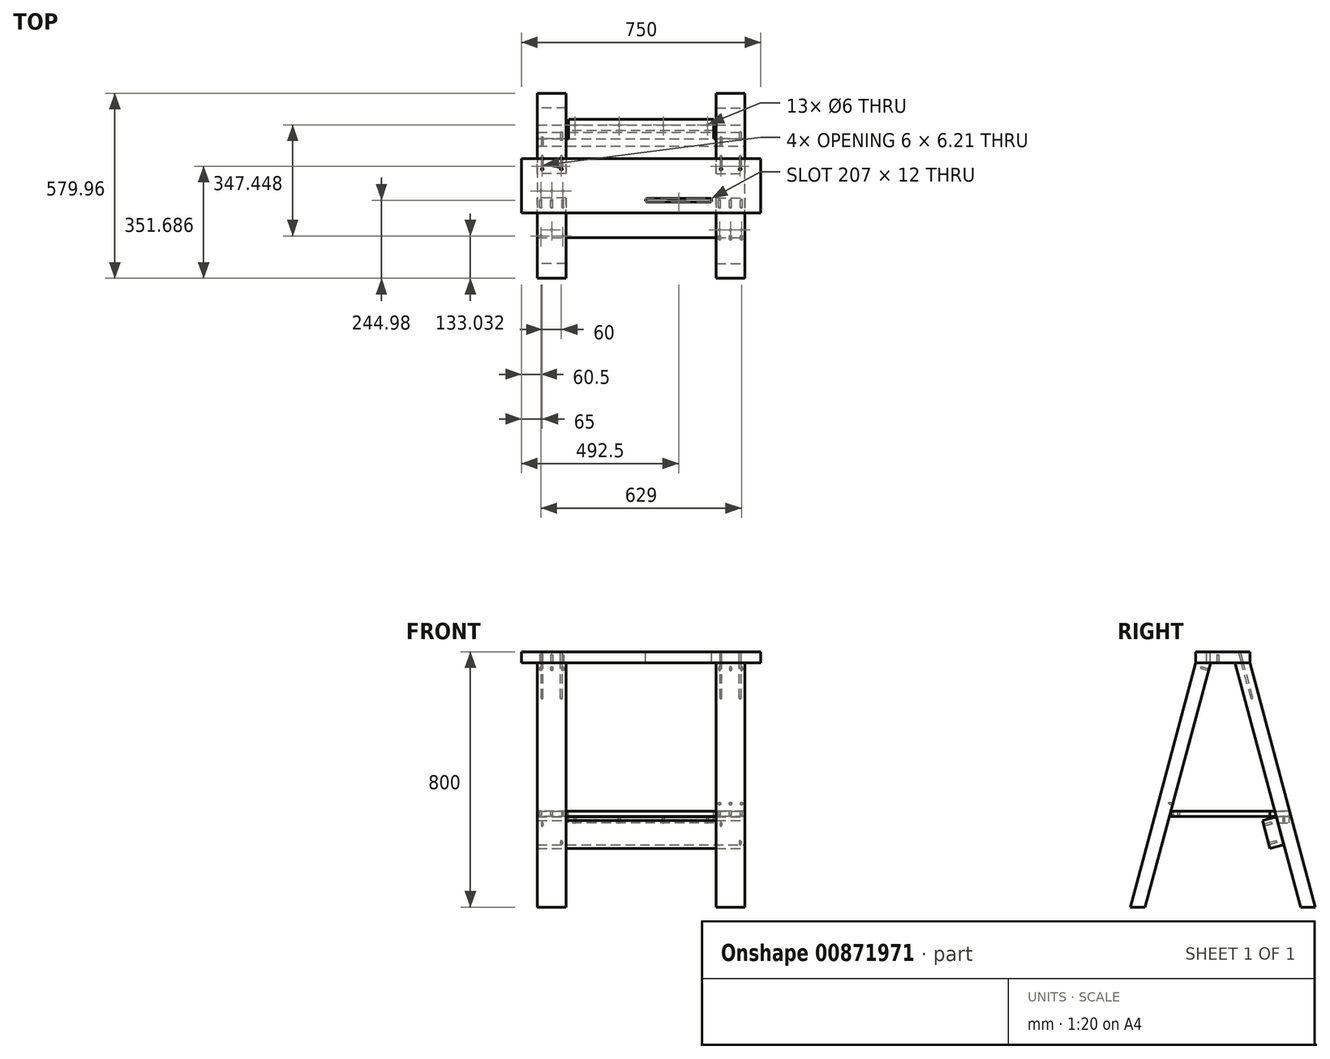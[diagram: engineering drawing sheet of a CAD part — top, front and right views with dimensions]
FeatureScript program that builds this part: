
annotation { "Feature Type Name" : "Feature", "Feature Type Description" : "" }
export const myFeature = defineFeature(function(context is Context, id is Id, definition is map)
    precondition{}
    {
        {
            var Q0;
            Q0=qCreatedBy(makeId("Right.planeOp"),FACE);
            var sketch = newSketch(context, id + "F0", { "sketchPlane" : qUnion([Q0])});
            skLineSegment(sketch, "E0.bottom", {"start": v(-85, -17.5) * mm, "end": v(85, -17.5) * mm});
            skLineSegment(sketch, "E0.top", {"start": v(-85, 17.5) * mm, "end": v(85, 17.5) * mm});
            skLineSegment(sketch, "E0.left", {"start": v(-85, -17.5) * mm, "end": v(-85, 17.5) * mm});
            skLineSegment(sketch, "E0.right", {"start": v(85, -17.5) * mm, "end": v(85, 17.5) * mm});
            skPoint(sketch, "E0.middle", {"position": v(0, 0) * mm});
            skSolve(sketch);
        }
        {
            var Q0;
            Q0=makeQuery(id+"F0.imprint","IMPRINT",FACE,{"disambiguationData":[TD([[makeQuery(id+"F0.imprint","IMPRINT",EDGE,{"derivedFrom":sQuery(id+"F0.wireOp",EDGE,"E0.bottom")}),1.0]])]});
            extrude(context, id + "F1", {"entities" : qUnion([Q0]), "endBound" : BoundingType.SYMMETRIC, "depth" : 750 * mm, "offsetDistance" : 25 * mm});
        }
        {
            var Q0;
            Q0=qCreatedBy(makeId("Front.planeOp"),FACE);
            var sketch = newSketch(context, id + "F2", { "sketchPlane" : qUnion([Q0])});
            skLineSegment(sketch, "E1", {"start": v(-325, -212.53) * mm, "end": v(-325, -17.5) * mm});
            skLineSegment(sketch, "E2", {"start": v(-325, -17.5) * mm, "end": v(-325, -257.51) * mm, "construction": true});
            skSolve(sketch);
        }
        {
            var Q0;
            Q0=qCreatedBy(makeId("Right.planeOp"),FACE);
            var Q1;
            Q1=sQuery(id+"F2.wireOp",EDGE,"E2");
            cPlane(context, id + "F3", {"entities" : qUnion([Q0, Q1]), "cplaneType" : CPlaneType.LINE_ANGLE, "offset" : 25 * mm, "angle" : 0 * degree, "width" : 150 * mm, "height" : 150 * mm});
        }
        {
            var Q0;
            Q0=qCreatedBy(id+"F3.planeOp",FACE);
            var sketch = newSketch(context, id + "F4", { "sketchPlane" : qUnion([Q0])});
            skLineSegment(sketch, "E3", {"start": v(-85, -17.5) * mm, "end": v(-289.98, -782.5) * mm});
            skLineSegment(sketch, "E4", {"start": v(-289.98, -782.5) * mm, "end": v(-243.4, -782.5) * mm});
            skLineSegment(sketch, "E5", {"start": v(-243.4, -782.5) * mm, "end": v(-38.41, -17.5) * mm});
            skLineSegment(sketch, "E6", {"start": v(-38.41, -17.5) * mm, "end": v(-85, -17.5) * mm});
            skLineSegment(sketch, "E7", {"start": v(0, 0) * mm, "end": v(0, -726.6) * mm, "construction": true});
            skSolve(sketch);
        }
        {
            var Q0;
            Q0 = qSketchRegion(id + "F4", true);
            extrude(context, id + "F5", {"entities" : qUnion([Q0]), "oppositeDirection" : true, "depth" : 90 * mm, "offsetDistance" : 25 * mm});
        }
        {
            var Q0;
            Q0=makeQuery(id+"F5.opExtrude","SWEPT_BODY",BODY,{"disambiguationData":[OSD([sQuery(id+"F4.wireOp",EDGE,"E3"),sQuery(id+"F4.wireOp",EDGE,"E4"),sQuery(id+"F4.wireOp",EDGE,"E5"),sQuery(id+"F4.wireOp",EDGE,"E6")])]});
            var Q1;
            Q1=qCreatedBy(makeId("Front.planeOp"),FACE);
            mirror(context, id + "F6", {"entities" : qUnion([Q0]), "mirrorPlane" : qUnion([Q1])});
        }
        {
            var Q0;
            Q0=makeQuery(id+"F6.opPattern","COPY",FACE,{"derivedFrom":makeQuery(id+"F5.opExtrude","SWEPT_FACE",FACE,{"disambiguationData":[OSD([sQuery(id+"F4.wireOp",EDGE,"E5")])]}),"instanceName":"1"});
            var sketch = newSketch(context, id + "F7", { "sketchPlane" : qUnion([Q0])});
            skPoint(sketch, "E8", {"position": v(245.5, -48.65) * mm});
            skPoint(sketch, "E9", {"position": v(280, -48.65) * mm});
            skPoint(sketch, "E10", {"position": v(314.5, -48.65) * mm});
            skLineSegment(sketch, "E11", {"start": v(280, -48.65) * mm, "end": v(245.5, -48.65) * mm, "construction": true});
            skLineSegment(sketch, "E12", {"start": v(280, -48.65) * mm, "end": v(314.5, -48.65) * mm, "construction": true});
            skLineSegment(sketch, "E13", {"start": v(280, -48.65) * mm, "end": v(280, -26.85) * mm, "construction": true});
            skSolve(sketch);
        }
        {
            var Q0;
            Q0=sQuery(id+"F7.wireOp",VERTEX,"E8");
            var Q1;
            Q1=sQuery(id+"F7.wireOp",VERTEX,"E9");
            var Q2;
            Q2=sQuery(id+"F7.wireOp",VERTEX,"E10");
            var Q3;
            Q3=makeQuery(id+"F6.opPattern","COPY",BODY,{"derivedFrom":makeQuery(id+"F5.opExtrude","SWEPT_BODY",BODY,{"disambiguationData":[OSD([sQuery(id+"F4.wireOp",EDGE,"E3"),sQuery(id+"F4.wireOp",EDGE,"E4"),sQuery(id+"F4.wireOp",EDGE,"E5"),sQuery(id+"F4.wireOp",EDGE,"E6")])]}),"instanceName":"1"});
            hole(context, id + "F8", {"style" : HoleStyle.SIMPLE, "endStyle" : HoleEndStyle.BLIND, "holeDiameter" : 6 * mm, "majorDiameter" : 5 * mm, "holeDepth" : 25 * mm, "isTappedThrough" : true, "tappedDepth" : 12 * mm, "tapClearance" : 3, "locations" : qUnion([Q0, Q1, Q2]), "scope" : qUnion([Q3])});
        }
        {
            var Q0;
            Q0=makeQuery(id+"F6.opPattern","COPY",BODY,{"derivedFrom":makeQuery(id+"F5.opExtrude","SWEPT_BODY",BODY,{"disambiguationData":[OSD([sQuery(id+"F4.wireOp",EDGE,"E3"),sQuery(id+"F4.wireOp",EDGE,"E4"),sQuery(id+"F4.wireOp",EDGE,"E5"),sQuery(id+"F4.wireOp",EDGE,"E6")])]}),"instanceName":"1"});
            var Q1;
            Q1=makeQuery(id+"F5.opExtrude","SWEPT_BODY",BODY,{"disambiguationData":[OSD([sQuery(id+"F4.wireOp",EDGE,"E3"),sQuery(id+"F4.wireOp",EDGE,"E4"),sQuery(id+"F4.wireOp",EDGE,"E5"),sQuery(id+"F4.wireOp",EDGE,"E6")])]});
            var Q2;
            Q2=qCreatedBy(makeId("Right.planeOp"),FACE);
            mirror(context, id + "F9", {"entities" : qUnion([Q0, Q1]), "mirrorPlane" : qUnion([Q2])});
        }
        {
            var Q0;
            Q0=makeQuery(id+"F1.opExtrude","SWEPT_FACE",FACE,{"disambiguationData":[OSD([sQuery(id+"F0.wireOp",EDGE,"E0.bottom")])]});
            var sketch = newSketch(context, id + "F10", { "sketchPlane" : qUnion([Q0])});
            skPoint(sketch, "E14", {"position": v(-245.5, 16) * mm});
            skPoint(sketch, "E15", {"position": v(-280, 16) * mm});
            skPoint(sketch, "E16", {"position": v(-314.5, 16) * mm});
            skLineSegment(sketch, "E17", {"start": v(-314.5, 16) * mm, "end": v(-314.5, 44.05) * mm, "construction": true});
            skLineSegment(sketch, "E18", {"start": v(-245.5, 44.05) * mm, "end": v(-245.5, 16) * mm, "construction": true});
            skLineSegment(sketch, "E19", {"start": v(-280, 16) * mm, "end": v(-280, 44.05) * mm, "construction": true});
            skLineSegment(sketch, "E20", {"start": v(-375, 0) * mm, "end": v(-119.6, 0) * mm, "construction": true});
            skSolve(sketch);
        }
        {
            var Q0;
            Q0=sQuery(id+"F10.wireOp",VERTEX,"E16");
            var Q1;
            Q1=sQuery(id+"F10.wireOp",VERTEX,"E15");
            var Q2;
            Q2=sQuery(id+"F10.wireOp",VERTEX,"E14");
            var Q3;
            Q3=makeQuery(id+"F1.opExtrude","SWEPT_BODY",BODY,{"disambiguationData":[OSD([sQuery(id+"F0.wireOp",EDGE,"E0.bottom"),sQuery(id+"F0.wireOp",EDGE,"E0.top"),sQuery(id+"F0.wireOp",EDGE,"E0.left"),sQuery(id+"F0.wireOp",EDGE,"E0.right")])]});
            hole(context, id + "F11", {"style" : HoleStyle.SIMPLE, "endStyle" : HoleEndStyle.BLIND, "holeDiameter" : 6 * mm, "majorDiameter" : 5 * mm, "holeDepth" : 25 * mm, "isTappedThrough" : true, "tappedDepth" : 12 * mm, "tapClearance" : 3, "locations" : qUnion([Q0, Q1, Q2]), "scope" : qUnion([Q3])});
        }
        {
            var Q0;
            Q0=qCreatedBy(makeId("Right.planeOp"),FACE);
            var sketch = newSketch(context, id + "F12", { "sketchPlane" : qUnion([Q0])});
            skLineSegment(sketch, "E21", {"start": v(-274.26, -482.5) * mm, "end": v(250.79, -482.5) * mm});
            skSolve(sketch);
        }
        {
            var Q0;
            Q0=sQuery(id+"F12.wireOp",EDGE,"E21");
            var Q1;
            Q1=qCreatedBy(makeId("Top.planeOp"),FACE);
            cPlane(context, id + "F13", {"entities" : qUnion([Q0, Q1]), "cplaneType" : CPlaneType.LINE_ANGLE, "offset" : 25 * mm, "angle" : 0 * degree, "width" : 150 * mm, "height" : 150 * mm});
        }
        {
            var Q0;
            Q0=qCreatedBy(id+"F13.planeOp",FACE);
            var sketch = newSketch(context, id + "F14", { "sketchPlane" : qUnion([Q0])});
            skLineSegment(sketch, "E22", {"start": v(-325, 162) * mm, "end": v(325, 162) * mm});
            skLineSegment(sketch, "E23", {"start": v(325, 162) * mm, "end": v(325, -148) * mm});
            skLineSegment(sketch, "E24", {"start": v(325, -148) * mm, "end": v(227.5, -148) * mm});
            skLineSegment(sketch, "E25", {"start": v(227.5, -148) * mm, "end": v(227.5, -208) * mm});
            skLineSegment(sketch, "E26", {"start": v(227.5, -208) * mm, "end": v(-227.5, -208) * mm});
            skLineSegment(sketch, "E27", {"start": v(-227.5, -208) * mm, "end": v(-227.5, -148) * mm});
            skLineSegment(sketch, "E28", {"start": v(-227.5, -148) * mm, "end": v(-325, -148) * mm});
            skLineSegment(sketch, "E29", {"start": v(-325, -148) * mm, "end": v(-325, 162) * mm});
            skLineSegment(sketch, "E30", {"start": v(0, 0) * mm, "end": v(0, 162) * mm, "construction": true});
            skSolve(sketch);
        }
        {
            var Q0;
            Q0 = qSketchRegion(id + "F14", true);
            extrude(context, id + "F15", {"entities" : qUnion([Q0]), "depth" : 16 * mm, "offsetDistance" : 25 * mm});
        }
        {
            var Q0;
            Q0=makeQuery(id+"F9.opPattern","COPY",FACE,{"derivedFrom":makeQuery(id+"F6.opPattern","COPY",FACE,{"derivedFrom":makeQuery(id+"F5.opExtrude","SWEPT_FACE",FACE,{"disambiguationData":[OSD([sQuery(id+"F4.wireOp",EDGE,"E5")])]}),"instanceName":"1"}),"instanceName":"1"});
            var sketch = newSketch(context, id + "F16", { "sketchPlane" : qUnion([Q0])});
            skLineSegment(sketch, "E31", {"start": v(-314.5, -484.83) * mm, "end": v(-280, -484.83) * mm, "construction": true});
            skLineSegment(sketch, "E32", {"start": v(-280, -484.83) * mm, "end": v(-245.5, -484.83) * mm, "construction": true});
            skLineSegment(sketch, "E33", {"start": v(-245.5, -484.83) * mm, "end": v(-245.5, -21.04) * mm, "construction": true});
            skLineSegment(sketch, "E34", {"start": v(-314.5, -21.04) * mm, "end": v(-314.5, -484.83) * mm, "construction": true});
            skSolve(sketch);
        }
        {
            var Q0;
            Q0=sQuery(id+"F16.wireOp",VERTEX,"E31.start");
            var Q1;
            Q1=sQuery(id+"F16.wireOp",VERTEX,"E31.end");
            var Q2;
            Q2=sQuery(id+"F16.wireOp",VERTEX,"E32.end");
            var Q3;
            Q3=makeQuery(id+"F9.opPattern","COPY",BODY,{"derivedFrom":makeQuery(id+"F6.opPattern","COPY",BODY,{"derivedFrom":makeQuery(id+"F5.opExtrude","SWEPT_BODY",BODY,{"disambiguationData":[OSD([sQuery(id+"F4.wireOp",EDGE,"E3"),sQuery(id+"F4.wireOp",EDGE,"E4"),sQuery(id+"F4.wireOp",EDGE,"E5"),sQuery(id+"F4.wireOp",EDGE,"E6")])]}),"instanceName":"1"}),"instanceName":"1"});
            var Q4;
            Q4=makeQuery(id+"F6.opPattern","COPY",BODY,{"derivedFrom":makeQuery(id+"F5.opExtrude","SWEPT_BODY",BODY,{"disambiguationData":[OSD([sQuery(id+"F4.wireOp",EDGE,"E3"),sQuery(id+"F4.wireOp",EDGE,"E4"),sQuery(id+"F4.wireOp",EDGE,"E5"),sQuery(id+"F4.wireOp",EDGE,"E6")])]}),"instanceName":"1"});
            hole(context, id + "F17", {"style" : HoleStyle.SIMPLE, "endStyle" : HoleEndStyle.BLIND, "holeDiameter" : 6 * mm, "majorDiameter" : 5 * mm, "holeDepth" : 12 * mm, "isTappedThrough" : true, "tappedDepth" : 12 * mm, "tapClearance" : 3, "locations" : qUnion([Q0, Q1, Q2]), "scope" : qUnion([Q3, Q4])});
        }
        {
            var Q0;
            Q0=makeQuery(id+"F15.opExtrude","CAP_FACE",FACE,{"disambiguationData":[OSD([sQuery(id+"F14.wireOp",EDGE,"E22"),sQuery(id+"F14.wireOp",EDGE,"E23"),sQuery(id+"F14.wireOp",EDGE,"E24"),sQuery(id+"F14.wireOp",EDGE,"E25"),sQuery(id+"F14.wireOp",EDGE,"E26"),sQuery(id+"F14.wireOp",EDGE,"E27"),sQuery(id+"F14.wireOp",EDGE,"E28"),sQuery(id+"F14.wireOp",EDGE,"E29")])],"isStart":true});
            var sketch = newSketch(context, id + "F18", { "sketchPlane" : qUnion([Q0])});
            skLineSegment(sketch, "E35", {"start": v(314.5, -138) * mm, "end": v(280, -138) * mm});
            skLineSegment(sketch, "E36", {"start": v(280, -138) * mm, "end": v(245.5, -138) * mm});
            skLineSegment(sketch, "E37", {"start": v(245.5, -138) * mm, "end": v(-245.5, -138) * mm});
            skLineSegment(sketch, "E38", {"start": v(-245.5, -138) * mm, "end": v(-280, -138) * mm});
            skLineSegment(sketch, "E39", {"start": v(-280, -138) * mm, "end": v(-314.5, -138) * mm});
            skLineSegment(sketch, "E40", {"start": v(314.5, -156.95) * mm, "end": v(314.5, -138) * mm});
            skLineSegment(sketch, "E41", {"start": v(245.5, -156.95) * mm, "end": v(245.5, -138) * mm});
            skLineSegment(sketch, "E42", {"start": v(-245.5, -156.95) * mm, "end": v(-245.5, -138) * mm});
            skLineSegment(sketch, "E43", {"start": v(-314.5, -156.95) * mm, "end": v(-314.5, -138) * mm});
            skSolve(sketch);
        }
        {
            var Q0;
            Q0=sQuery(id+"F18.wireOp",VERTEX,"E43.start");
            var Q1;
            Q1=sQuery(id+"F18.wireOp",VERTEX,"E38.end");
            var Q2;
            Q2=sQuery(id+"F18.wireOp",VERTEX,"E42.start");
            var Q3;
            Q3=sQuery(id+"F18.wireOp",VERTEX,"E37.start");
            var Q4;
            Q4=sQuery(id+"F18.wireOp",VERTEX,"E36.start");
            var Q5;
            Q5=sQuery(id+"F18.wireOp",VERTEX,"E35.start");
            var Q6;
            Q6=makeQuery(id+"F15.opExtrude","SWEPT_BODY",BODY,{"disambiguationData":[OSD([sQuery(id+"F14.wireOp",EDGE,"E22"),sQuery(id+"F14.wireOp",EDGE,"E23"),sQuery(id+"F14.wireOp",EDGE,"E24"),sQuery(id+"F14.wireOp",EDGE,"E25"),sQuery(id+"F14.wireOp",EDGE,"E26"),sQuery(id+"F14.wireOp",EDGE,"E27"),sQuery(id+"F14.wireOp",EDGE,"E28"),sQuery(id+"F14.wireOp",EDGE,"E29")])]});
            hole(context, id + "F19", {"style" : HoleStyle.SIMPLE, "endStyle" : HoleEndStyle.BLIND, "holeDiameter" : 6 * mm, "majorDiameter" : 5 * mm, "holeDepth" : 12 * mm, "isTappedThrough" : true, "tappedDepth" : 12 * mm, "tapClearance" : 3, "locations" : qUnion([Q0, Q1, Q2, Q3, Q4, Q5]), "scope" : qUnion([Q6])});
        }
        {
            var Q0;
            Q0=makeQuery(id+"F5.opExtrude","SWEPT_FACE",FACE,{"disambiguationData":[OSD([sQuery(id+"F4.wireOp",EDGE,"E5")])]});
            var sketch = newSketch(context, id + "F20", { "sketchPlane" : qUnion([Q0])});
            skLineSegment(sketch, "E44.bottom", {"start": v(-325, -526.33) * mm, "end": v(325, -526.33) * mm});
            skLineSegment(sketch, "E44.top", {"start": v(-325, -616.33) * mm, "end": v(325, -616.33) * mm});
            skLineSegment(sketch, "E44.left", {"start": v(-325, -526.33) * mm, "end": v(-325, -616.33) * mm});
            skLineSegment(sketch, "E44.right", {"start": v(325, -526.33) * mm, "end": v(325, -616.33) * mm});
            skSolve(sketch);
        }
        {
            var Q0;
            {var subQ0=sQuery(id+"F20.wireOp",EDGE,"E44.right");Q0=makeQuery(id+"F20.imprint","IMPRINT",FACE,{"disambiguationData":[TD([[makeQuery(id+"F20.imprint","IMPRINT",EDGE,{"derivedFrom":subQ0}),-1.0]])]});}
            var Q1;
            {var subQ0=sQuery(id+"F20.wireOp",EDGE,"E44.left");Q1=makeQuery(id+"F20.imprint","IMPRINT",FACE,{"disambiguationData":[TD([[makeQuery(id+"F20.imprint","IMPRINT",EDGE,{"derivedFrom":subQ0}),-1.0]])]});}
            extrude(context, id + "F21", {"entities" : qUnion([Q0, Q1]), "depth" : 45 * mm, "offsetDistance" : 25 * mm});
        }
        {
            var Q0;
            Q0=makeQuery(id+"F15.opExtrude","CAP_FACE",FACE,{"disambiguationData":[OSD([sQuery(id+"F14.wireOp",EDGE,"E22"),sQuery(id+"F14.wireOp",EDGE,"E23"),sQuery(id+"F14.wireOp",EDGE,"E24"),sQuery(id+"F14.wireOp",EDGE,"E25"),sQuery(id+"F14.wireOp",EDGE,"E26"),sQuery(id+"F14.wireOp",EDGE,"E27"),sQuery(id+"F14.wireOp",EDGE,"E28"),sQuery(id+"F14.wireOp",EDGE,"E29")])],"isStart":false});
            var sketch = newSketch(context, id + "F22", { "sketchPlane" : qUnion([Q0])});
            skLineSegment(sketch, "E45.bottom", {"start": v(227.5, -208) * mm, "end": v(-227.5, -208) * mm});
            skLineSegment(sketch, "E45.top", {"start": v(227.5, -173) * mm, "end": v(-227.5, -173) * mm});
            skLineSegment(sketch, "E45.left", {"start": v(227.5, -208) * mm, "end": v(227.5, -173) * mm});
            skLineSegment(sketch, "E45.right", {"start": v(-227.5, -208) * mm, "end": v(-227.5, -173) * mm});
            skSolve(sketch);
        }
        {
            var Q0;
            Q0 = qSketchRegion(id + "F22", true);
            extrude(context, id + "F23", {"entities" : qUnion([Q0]), "depth" : 20 * mm, "offsetDistance" : 25 * mm});
        }
        {
            var Q0;
            Q0=makeQuery(id+"F21.opExtrude","CAP_FACE",FACE,{"disambiguationData":[OSD([sQuery(id+"F4.wireOp",EDGE,"E5"),sQuery(id+"F20.wireOp",EDGE,"E44.bottom"),sQuery(id+"F20.wireOp",EDGE,"E44.top"),sQuery(id+"F20.wireOp",EDGE,"E44.right")])],"isStart":false});
            var sketch = newSketch(context, id + "F24", { "sketchPlane" : qUnion([Q0])});
            skLineSegment(sketch, "E46", {"start": v(250, -541.33) * mm, "end": v(310, -601.33) * mm});
            skLineSegment(sketch, "E47", {"start": v(-310, -541.33) * mm, "end": v(-250, -601.33) * mm});
            skSolve(sketch);
        }
        {
            var Q0;
            Q0=sQuery(id+"F24.wireOp",VERTEX,"E46.start");
            var Q1;
            Q1=sQuery(id+"F24.wireOp",VERTEX,"E46.end");
            var Q2;
            Q2=sQuery(id+"F24.wireOp",VERTEX,"E47.start");
            var Q3;
            Q3=sQuery(id+"F24.wireOp",VERTEX,"E47.end");
            var Q4;
            Q4=makeQuery(id+"F21.opExtrude","SWEPT_BODY",BODY,{"disambiguationData":[OSD([sQuery(id+"F4.wireOp",EDGE,"E5"),sQuery(id+"F20.wireOp",EDGE,"E44.bottom"),sQuery(id+"F20.wireOp",EDGE,"E44.top"),sQuery(id+"F20.wireOp",EDGE,"E44.right")])]});
            hole(context, id + "F25", {"style" : HoleStyle.SIMPLE, "endStyle" : HoleEndStyle.BLIND, "holeDiameter" : 6 * mm, "majorDiameter" : 5 * mm, "holeDepth" : 25 * mm, "isTappedThrough" : true, "tappedDepth" : 12 * mm, "tapClearance" : 3, "locations" : qUnion([Q0, Q1, Q2, Q3]), "scope" : qUnion([Q4])});
        }
        {
            var Q0;
            Q0=makeQuery(id+"F23.opExtrude","CAP_FACE",FACE,{"disambiguationData":[OSD([sQuery(id+"F22.wireOp",EDGE,"E45.bottom"),sQuery(id+"F22.wireOp",EDGE,"E45.top"),sQuery(id+"F22.wireOp",EDGE,"E45.left"),sQuery(id+"F22.wireOp",EDGE,"E45.right")])],"isStart":false});
            var sketch = newSketch(context, id + "F26", { "sketchPlane" : qUnion([Q0])});
            skLineSegment(sketch, "E48", {"start": v(207.5, -190.5) * mm, "end": v(69.17, -190.5) * mm});
            skLineSegment(sketch, "E49", {"start": v(69.17, -190.5) * mm, "end": v(-69.17, -190.5) * mm});
            skLineSegment(sketch, "E50", {"start": v(-69.17, -190.5) * mm, "end": v(-207.5, -190.5) * mm});
            skSolve(sketch);
        }
        {
            var Q0;
            Q0=sQuery(id+"F26.wireOp",VERTEX,"E48.start");
            var Q1;
            Q1=sQuery(id+"F26.wireOp",VERTEX,"E48.end");
            var Q2;
            Q2=sQuery(id+"F26.wireOp",VERTEX,"E49.end");
            var Q3;
            Q3=sQuery(id+"F26.wireOp",VERTEX,"E50.end");
            var Q4;
            Q4=makeQuery(id+"F15.opExtrude","SWEPT_BODY",BODY,{"disambiguationData":[OSD([sQuery(id+"F14.wireOp",EDGE,"E22"),sQuery(id+"F14.wireOp",EDGE,"E23"),sQuery(id+"F14.wireOp",EDGE,"E24"),sQuery(id+"F14.wireOp",EDGE,"E25"),sQuery(id+"F14.wireOp",EDGE,"E26"),sQuery(id+"F14.wireOp",EDGE,"E27"),sQuery(id+"F14.wireOp",EDGE,"E28"),sQuery(id+"F14.wireOp",EDGE,"E29")])]});
            var Q5;
            Q5=makeQuery(id+"F23.opExtrude","SWEPT_BODY",BODY,{"disambiguationData":[OSD([sQuery(id+"F22.wireOp",EDGE,"E45.bottom"),sQuery(id+"F22.wireOp",EDGE,"E45.top"),sQuery(id+"F22.wireOp",EDGE,"E45.left"),sQuery(id+"F22.wireOp",EDGE,"E45.right")])]});
            hole(context, id + "F27", {"style" : HoleStyle.SIMPLE, "endStyle" : HoleEndStyle.BLIND, "holeDiameter" : 6 * mm, "majorDiameter" : 5 * mm, "holeDepth" : 20 * mm, "isTappedThrough" : true, "tappedDepth" : 12 * mm, "tapClearance" : 3, "locations" : qUnion([Q0, Q1, Q2, Q3]), "scope" : qUnion([Q4, Q5])});
        }
        {
            var Q0;
            Q0=qCreatedBy(makeId("Right.planeOp"),FACE);
            var sketch = newSketch(context, id + "F28", { "sketchPlane" : qUnion([Q0])});
            skLineSegment(sketch, "E51", {"start": v(29.03, 17.5) * mm, "end": v(72.5, 29.15) * mm, "construction": true});
            skSolve(sketch);
        }
        {
            var Q0;
            Q0=sQuery(id+"F28.wireOp",EDGE,"E51");
            var Q1;
            Q1=qCreatedBy(makeId("Front.planeOp"),FACE);
            cPlane(context, id + "F29", {"entities" : qUnion([Q0, Q1]), "cplaneType" : CPlaneType.LINE_ANGLE, "offset" : 25 * mm, "angle" : 0 * degree, "width" : 150 * mm, "height" : 150 * mm});
        }
        {
            var Q0;
            Q0=qCreatedBy(id+"F29.planeOp",FACE);
            var sketch = newSketch(context, id + "F30", { "sketchPlane" : qUnion([Q0])});
            skLineSegment(sketch, "E52", {"start": v(250, -55.07) * mm, "end": v(310, -55.07) * mm});
            skLineSegment(sketch, "E53", {"start": v(250, -55.07) * mm, "end": v(-250, -55.07) * mm});
            skLineSegment(sketch, "E54", {"start": v(-250, -55.07) * mm, "end": v(-310, -55.07) * mm});
            skSolve(sketch);
        }
        {
            var Q0;
            Q0=sQuery(id+"F30.wireOp",VERTEX,"E52.end");
            var Q1;
            Q1=sQuery(id+"F30.wireOp",VERTEX,"E53.start");
            var Q2;
            Q2=sQuery(id+"F30.wireOp",VERTEX,"E53.end");
            var Q3;
            Q3=sQuery(id+"F30.wireOp",VERTEX,"E54.end");
            var Q4;
            Q4=makeQuery(id+"F9.opPattern","COPY",BODY,{"derivedFrom":makeQuery(id+"F5.opExtrude","SWEPT_BODY",BODY,{"disambiguationData":[OSD([sQuery(id+"F4.wireOp",EDGE,"E3"),sQuery(id+"F4.wireOp",EDGE,"E4"),sQuery(id+"F4.wireOp",EDGE,"E5"),sQuery(id+"F4.wireOp",EDGE,"E6")])]}),"instanceName":"1"});
            var Q5;
            Q5=makeQuery(id+"F1.opExtrude","SWEPT_BODY",BODY,{"disambiguationData":[OSD([sQuery(id+"F0.wireOp",EDGE,"E0.bottom"),sQuery(id+"F0.wireOp",EDGE,"E0.top"),sQuery(id+"F0.wireOp",EDGE,"E0.left"),sQuery(id+"F0.wireOp",EDGE,"E0.right")])]});
            var Q6;
            Q6=makeQuery(id+"F5.opExtrude","SWEPT_BODY",BODY,{"disambiguationData":[OSD([sQuery(id+"F4.wireOp",EDGE,"E3"),sQuery(id+"F4.wireOp",EDGE,"E4"),sQuery(id+"F4.wireOp",EDGE,"E5"),sQuery(id+"F4.wireOp",EDGE,"E6")])]});
            hole(context, id + "F31", {"style" : HoleStyle.SIMPLE, "endStyle" : HoleEndStyle.BLIND, "oppositeDirection" : true, "holeDiameter" : 6 * mm, "majorDiameter" : 5 * mm, "holeDepth" : 150 * mm, "isTappedThrough" : true, "tappedDepth" : 12 * mm, "tapClearance" : 3, "locations" : qUnion([Q0, Q1, Q2, Q3]), "scope" : qUnion([Q4, Q5, Q6])});
        }
        {
            var Q0;
            Q0=makeQuery(id+"F1.opExtrude","SWEPT_FACE",FACE,{"disambiguationData":[OSD([sQuery(id+"F0.wireOp",EDGE,"E0.top")])]});
            var sketch = newSketch(context, id + "F32", { "sketchPlane" : qUnion([Q0])});
            skLineSegment(sketch, "E55", {"start": v(215, -51) * mm, "end": v(20, -51) * mm});
            skArc(sketch, "E56", {"start": v(20, -39) * mm, "mid": v(14, -45) * mm, "end": v(20, -51) * mm});
            skLineSegment(sketch, "E57", {"start": v(20, -39) * mm, "end": v(215, -39) * mm});
            skArc(sketch, "E58", {"start": v(215, -51) * mm, "mid": v(221, -45) * mm, "end": v(215, -39) * mm});
            skSolve(sketch);
        }
        {
            var Q0;
            Q0 = qSketchRegion(id + "F32", true);
            extrude(context, id + "F33", {"entities" : qUnion([Q0]), "operationType" : NewBodyOperationType.REMOVE, "endBound" : BoundingType.UP_TO_NEXT, "oppositeDirection" : true, "depth" : 25 * mm, "offsetDistance" : 25 * mm});
        }
    });
